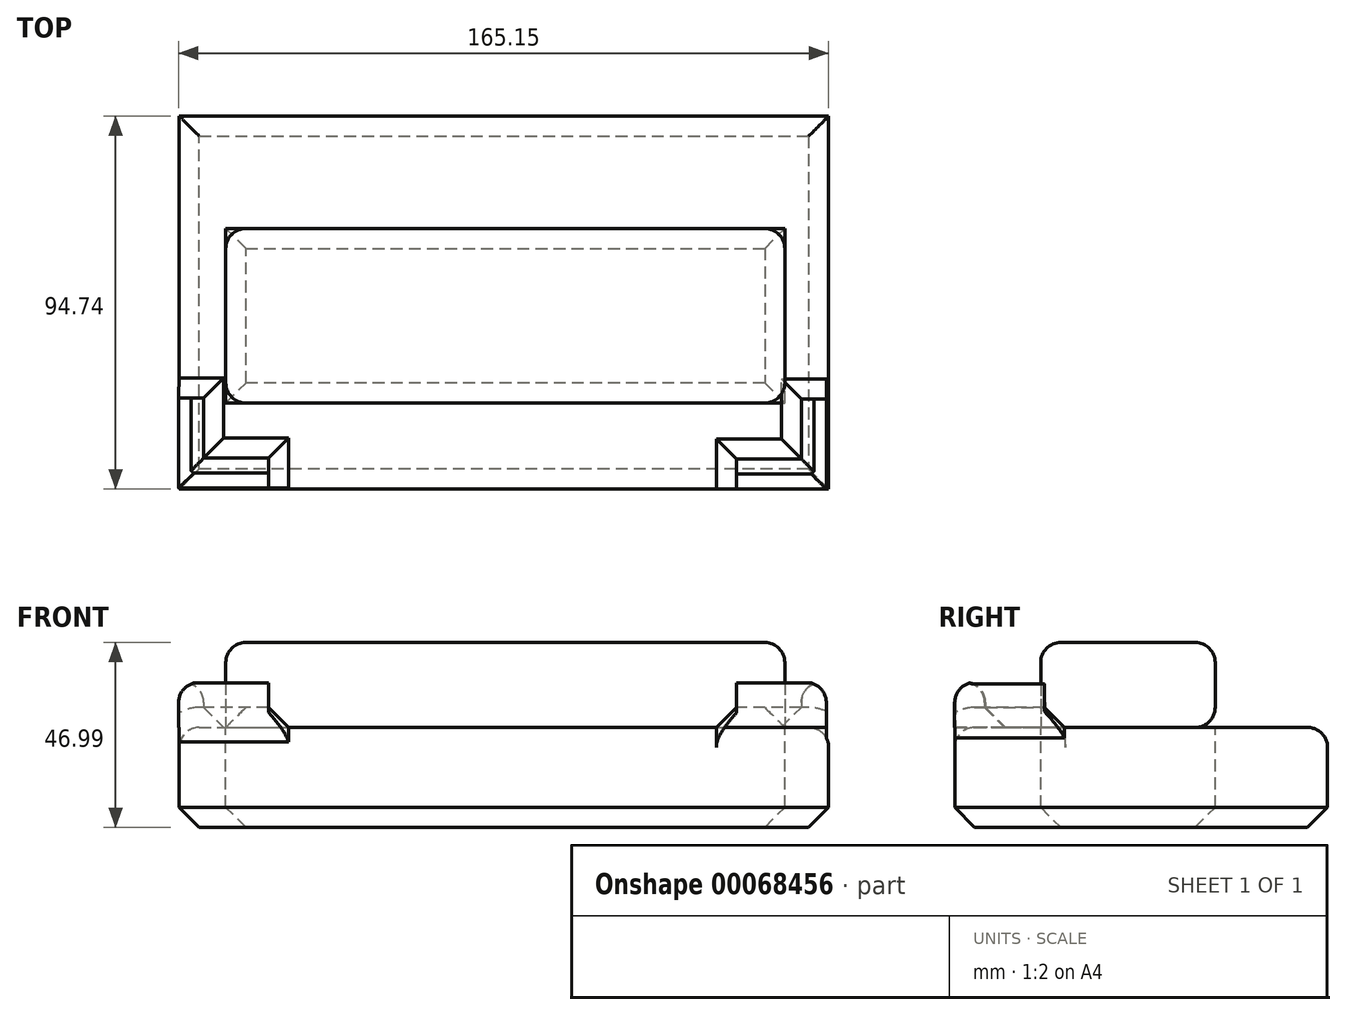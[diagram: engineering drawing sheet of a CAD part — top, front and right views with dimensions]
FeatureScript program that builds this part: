
annotation { "Feature Type Name" : "Feature", "Feature Type Description" : "" }
export const myFeature = defineFeature(function(context is Context, id is Id, definition is map)
    precondition{}
    {
        {
            var Q0;
            Q0=qCreatedBy(makeId("Top.planeOp"),FACE);
            var sketch = newSketch(context, id + "F0", { "sketchPlane" : qUnion([Q0])});
            skLineSegment(sketch, "E0.bottom", {"start": v(-81.55, 40.74) * mm, "end": v(83.45, 40.74) * mm});
            skLineSegment(sketch, "E0.top", {"start": v(-81.55, -53.99) * mm, "end": v(83.45, -53.99) * mm});
            skLineSegment(sketch, "E0.left", {"start": v(-81.55, 40.74) * mm, "end": v(-81.55, -53.99) * mm});
            skLineSegment(sketch, "E0.right", {"start": v(83.45, 40.74) * mm, "end": v(83.45, -53.99) * mm});
            skSolve(sketch);
        }
        {
            var Q0;
            Q0=qCreatedBy(makeId("Top.planeOp"),FACE);
            var sketch = newSketch(context, id + "F1", { "sketchPlane" : qUnion([Q0])});
            skLineSegment(sketch, "E1.bottom", {"start": v(-69.7, -32.12) * mm, "end": v(72.3, -32.12) * mm});
            skLineSegment(sketch, "E1.top", {"start": v(-69.7, 12.18) * mm, "end": v(72.3, 12.18) * mm});
            skLineSegment(sketch, "E1.left", {"start": v(-69.7, -32.12) * mm, "end": v(-69.7, 12.18) * mm});
            skLineSegment(sketch, "E1.right", {"start": v(72.3, -32.12) * mm, "end": v(72.3, 12.18) * mm});
            skSolve(sketch);
        }
        {
            var Q0;
            Q0=makeQuery(id+"F1.imprint","IMPRINT",FACE,{"disambiguationData":[TD([[makeQuery(id+"F1.imprint","IMPRINT",EDGE,{"derivedFrom":sQuery(id+"F1.wireOp",EDGE,"E1.bottom")}),1.0]])]});
            var Q1;
            Q1=makeQuery(id+"F0.imprint","IMPRINT",FACE,{"disambiguationData":[TD([[makeQuery(id+"F0.imprint","IMPRINT",EDGE,{"derivedFrom":sQuery(id+"F0.wireOp",EDGE,"E0.bottom")}),-1.0]])]});
            extrude(context, id + "F2", {"entities" : qUnion([Q0, Q1]), "oppositeDirection" : true, "depth" : 25.4 * mm});
        }
        {
            var Q0;
            Q0 = qSketchRegion(id + "F1", true);
            extrude(context, id + "F3", {"entities" : qUnion([Q0]), "depth" : 21.59 * mm});
        }
        {
            var Q0;
            Q0=qCreatedBy(makeId("Top.planeOp"),FACE);
            var sketch = newSketch(context, id + "F4", { "sketchPlane" : qUnion([Q0])});
            skLineSegment(sketch, "E2.bottom", {"start": v(82.84, -54) * mm, "end": v(59.98, -54) * mm});
            skLineSegment(sketch, "E2.top", {"start": v(82.84, -46.38) * mm, "end": v(59.98, -46.38) * mm});
            skLineSegment(sketch, "E2.left", {"start": v(82.84, -54) * mm, "end": v(82.84, -46.38) * mm});
            skLineSegment(sketch, "E2.right", {"start": v(59.98, -54) * mm, "end": v(59.98, -46.38) * mm});
            skLineSegment(sketch, "E3.bottom", {"start": v(82.84, -46.38) * mm, "end": v(76.5, -46.38) * mm});
            skLineSegment(sketch, "E3.top", {"start": v(82.84, -31.14) * mm, "end": v(76.5, -31.14) * mm});
            skLineSegment(sketch, "E3.left", {"start": v(82.84, -46.38) * mm, "end": v(82.84, -31.14) * mm});
            skLineSegment(sketch, "E3.right", {"start": v(76.5, -46.38) * mm, "end": v(76.5, -31.14) * mm});
            skLineSegment(sketch, "E4.bottom", {"start": v(-81.7, -53.8) * mm, "end": v(-58.84, -53.8) * mm});
            skLineSegment(sketch, "E4.top", {"start": v(-81.7, -46.18) * mm, "end": v(-58.84, -46.18) * mm});
            skLineSegment(sketch, "E4.left", {"start": v(-81.7, -53.8) * mm, "end": v(-81.7, -46.18) * mm});
            skLineSegment(sketch, "E4.right", {"start": v(-58.84, -53.8) * mm, "end": v(-58.84, -46.18) * mm});
            skLineSegment(sketch, "E5.bottom", {"start": v(-81.7, -46.18) * mm, "end": v(-75.35, -46.18) * mm});
            skLineSegment(sketch, "E5.top", {"start": v(-81.7, -30.94) * mm, "end": v(-75.35, -30.94) * mm});
            skLineSegment(sketch, "E5.left", {"start": v(-81.7, -46.18) * mm, "end": v(-81.7, -30.94) * mm});
            skLineSegment(sketch, "E5.right", {"start": v(-75.35, -46.18) * mm, "end": v(-75.35, -30.94) * mm});
            skSolve(sketch);
        }
        {
            var Q0;
            Q0 = qSketchRegion(id + "F4", true);
            extrude(context, id + "F5", {"entities" : qUnion([Q0]), "operationType" : NewBodyOperationType.ADD, "depth" : 11.43 * mm});
        }
        {
            var Q0;
            Q0=makeQuery(id+"F5.opExtrude","CAP_EDGE",EDGE,{"disambiguationData":[OSD([sQuery(id+"F4.wireOp",EDGE,"E2.top")])],"isStart":false});
            var Q1;
            Q1=makeQuery(id+"F5.opExtrude","CAP_EDGE",EDGE,{"disambiguationData":[OSD([sQuery(id+"F4.wireOp",EDGE,"E3.right")])],"isStart":false});
            var Q2;
            Q2=makeQuery(id+"F5.opExtrude","CAP_EDGE",EDGE,{"disambiguationData":[OSD([sQuery(id+"F4.wireOp",EDGE,"E4.top")])],"isStart":false});
            var Q3;
            Q3=makeQuery(id+"F5.opExtrude","CAP_EDGE",EDGE,{"disambiguationData":[OSD([sQuery(id+"F4.wireOp",EDGE,"E5.right")])],"isStart":false});
            var Q4;
            Q4=makeQuery(id+"F3.opExtrude","CAP_EDGE",EDGE,{"disambiguationData":[OSD([sQuery(id+"F1.wireOp",EDGE,"E1.bottom")])],"isStart":false});
            var Q5;
            Q5=makeQuery(id+"F3.opExtrude","CAP_EDGE",EDGE,{"disambiguationData":[OSD([sQuery(id+"F1.wireOp",EDGE,"E1.left")])],"isStart":false});
            var Q6;
            Q6=makeQuery(id+"F3.opExtrude","CAP_EDGE",EDGE,{"disambiguationData":[OSD([sQuery(id+"F1.wireOp",EDGE,"E1.top")])],"isStart":false});
            var Q7;
            Q7=makeQuery(id+"F3.opExtrude","CAP_EDGE",EDGE,{"disambiguationData":[OSD([sQuery(id+"F1.wireOp",EDGE,"E1.top")])],"isStart":true});
            var Q8;
            Q8=makeQuery(id+"F3.opExtrude","SWEPT_EDGE",EDGE,{"disambiguationData":[OSD([sQuery(id+"F1.wireOp",EDGE,"E1.bottom"),sQuery(id+"F1.wireOp",EDGE,"E1.right")])]});
            var Q9;
            Q9=makeQuery(id+"F3.opExtrude","SWEPT_EDGE",EDGE,{"disambiguationData":[OSD([sQuery(id+"F1.wireOp",EDGE,"E1.bottom"),sQuery(id+"F1.wireOp",EDGE,"E1.left")])]});
            var Q10;
            Q10=makeQuery(id+"F3.opExtrude","SWEPT_EDGE",EDGE,{"disambiguationData":[OSD([sQuery(id+"F1.wireOp",EDGE,"E1.top"),sQuery(id+"F1.wireOp",EDGE,"E1.left")])]});
            var Q11;
            Q11=makeQuery(id+"F3.opExtrude","SWEPT_EDGE",EDGE,{"disambiguationData":[OSD([sQuery(id+"F1.wireOp",EDGE,"E1.top"),sQuery(id+"F1.wireOp",EDGE,"E1.right")])]});
            var Q12;
            Q12=makeQuery(id+"F3.opExtrude","CAP_EDGE",EDGE,{"disambiguationData":[OSD([sQuery(id+"F1.wireOp",EDGE,"E1.right")])],"isStart":false});
            var Q13;
            Q13=makeQuery(id+"F2.opExtrude","CAP_EDGE",EDGE,{"disambiguationData":[OSD([sQuery(id+"F0.wireOp",EDGE,"E0.right")])],"isStart":true});
            var Q14;
            Q14=makeQuery(id+"F2.opExtrude","CAP_EDGE",EDGE,{"disambiguationData":[OSD([sQuery(id+"F0.wireOp",EDGE,"E0.bottom")])],"isStart":true});
            var Q15;
            {var subQ0=sQuery(id+"F0.wireOp",EDGE,"E0.left");var subQ1=sQuery(id+"F4.wireOp",EDGE,"E5.top");var subQ2=sQuery(id+"F0.wireOp",EDGE,"E0.bottom");Q15=makeQuery(id+"F5.boolean.opBoolean","SPLIT",EDGE,{"disambiguationData":[TD([makeQuery(id+"F2.opExtrude","SWEPT_FACE",FACE,{"disambiguationData":[OSD([subQ2])]}),makeQuery(id+"F2.opExtrude","CAP_FACE",FACE,{"disambiguationData":[OSD([subQ2,sQuery(id+"F0.wireOp",EDGE,"E0.top"),subQ0,sQuery(id+"F0.wireOp",EDGE,"E0.right")])],"isStart":true}),makeQuery(id+"F2.opExtrude","SWEPT_FACE",FACE,{"disambiguationData":[OSD([subQ0])]}),makeQuery(id+"F5.opExtrude","CAP_FACE",FACE,{"disambiguationData":[OSD([sQuery(id+"F4.wireOp",EDGE,"E4.bottom"),sQuery(id+"F4.wireOp",EDGE,"E4.top"),sQuery(id+"F4.wireOp",EDGE,"E4.left"),sQuery(id+"F4.wireOp",EDGE,"E4.right"),subQ1,sQuery(id+"F4.wireOp",EDGE,"E5.left"),sQuery(id+"F4.wireOp",EDGE,"E5.right")])],"isStart":true}),makeQuery(id+"F5.opExtrude","SWEPT_FACE",FACE,{"disambiguationData":[OSD([subQ1])]})])],"derivedFrom":makeQuery(id+"F2.opExtrude","CAP_EDGE",EDGE,{"disambiguationData":[OSD([subQ0])],"isStart":true})});}
            var Q16;
            {var subQ0=sQuery(id+"F4.wireOp",EDGE,"E2.right");var subQ1=sQuery(id+"F0.wireOp",EDGE,"E0.left");var subQ2=sQuery(id+"F0.wireOp",EDGE,"E0.top");Q16=makeQuery(id+"F5.boolean.opBoolean","SPLIT",EDGE,{"disambiguationData":[TD([makeQuery(id+"F2.opExtrude","CAP_FACE",FACE,{"disambiguationData":[OSD([sQuery(id+"F0.wireOp",EDGE,"E0.bottom"),subQ2,subQ1,sQuery(id+"F0.wireOp",EDGE,"E0.right")])],"isStart":true}),makeQuery(id+"F2.opExtrude","SWEPT_FACE",FACE,{"disambiguationData":[OSD([subQ2])]}),makeQuery(id+"F2.opExtrude","SWEPT_FACE",FACE,{"disambiguationData":[OSD([subQ1])]}),makeQuery(id+"F5.opExtrude","CAP_FACE",FACE,{"disambiguationData":[OSD([sQuery(id+"F4.wireOp",EDGE,"E2.bottom"),sQuery(id+"F4.wireOp",EDGE,"E2.top"),sQuery(id+"F4.wireOp",EDGE,"E2.left"),subQ0,sQuery(id+"F4.wireOp",EDGE,"E3.top"),sQuery(id+"F4.wireOp",EDGE,"E3.left"),sQuery(id+"F4.wireOp",EDGE,"E3.right")])],"isStart":true}),makeQuery(id+"F5.opExtrude","SWEPT_FACE",FACE,{"disambiguationData":[OSD([subQ0])]})])],"derivedFrom":makeQuery(id+"F2.opExtrude","CAP_EDGE",EDGE,{"disambiguationData":[OSD([subQ2])],"isStart":true})});}
            var Q17;
            Q17=makeQuery(id+"F5.opExtrude","CAP_EDGE",EDGE,{"disambiguationData":[OSD([sQuery(id+"F4.wireOp",EDGE,"E2.bottom")])],"isStart":false});
            var Q18;
            Q18=makeQuery(id+"F5.opExtrude","CAP_EDGE",EDGE,{"disambiguationData":[OSD([sQuery(id+"F4.wireOp",EDGE,"E4.bottom")])],"isStart":false});
            var Q19;
            Q19=makeQuery(id+"F5.opExtrude","CAP_EDGE",EDGE,{"disambiguationData":[OSD([sQuery(id+"F4.wireOp",EDGE,"E2.left"),sQuery(id+"F4.wireOp",EDGE,"E3.left")])],"isStart":false});
            var Q20;
            Q20=makeQuery(id+"F5.opExtrude","CAP_EDGE",EDGE,{"disambiguationData":[OSD([sQuery(id+"F4.wireOp",EDGE,"E4.left"),sQuery(id+"F4.wireOp",EDGE,"E5.left")])],"isStart":false});
            fillet(context, id + "F6", {"entities" : qUnion([Q0, Q1, Q2, Q3, Q4, Q5, Q6, Q7, Q8, Q9, Q10, Q11, Q12, Q13, Q14, Q15, Q16, Q17, Q18, Q19, Q20]), "radius" : 5.08 * mm, "tangentPropagation" : true, "allowEdgeOverflow" : false});
        }
        {
            var Q0;
            Q0=makeQuery(id+"F2.opExtrude","CAP_FACE",FACE,{"disambiguationData":[OSD([sQuery(id+"F0.wireOp",EDGE,"E0.bottom"),sQuery(id+"F0.wireOp",EDGE,"E0.top"),sQuery(id+"F0.wireOp",EDGE,"E0.left"),sQuery(id+"F0.wireOp",EDGE,"E0.right")])],"isStart":true});
            var Q1;
            Q1=makeQuery(id+"F2.opExtrude","CAP_FACE",FACE,{"disambiguationData":[OSD([sQuery(id+"F0.wireOp",EDGE,"E0.bottom"),sQuery(id+"F0.wireOp",EDGE,"E0.top"),sQuery(id+"F0.wireOp",EDGE,"E0.left"),sQuery(id+"F0.wireOp",EDGE,"E0.right")])],"isStart":false});
            var Q2;
            Q2=makeQuery(id+"F2.opExtrude","CAP_FACE",FACE,{"disambiguationData":[OSD([sQuery(id+"F1.wireOp",EDGE,"E1.bottom"),sQuery(id+"F1.wireOp",EDGE,"E1.top"),sQuery(id+"F1.wireOp",EDGE,"E1.left"),sQuery(id+"F1.wireOp",EDGE,"E1.right")])],"isStart":false});
            chamfer(context, id + "F7", {"entities" : qUnion([Q0, Q1, Q2]), "width" : 5.08 * mm, "tangentPropagation" : true});
        }
    });
